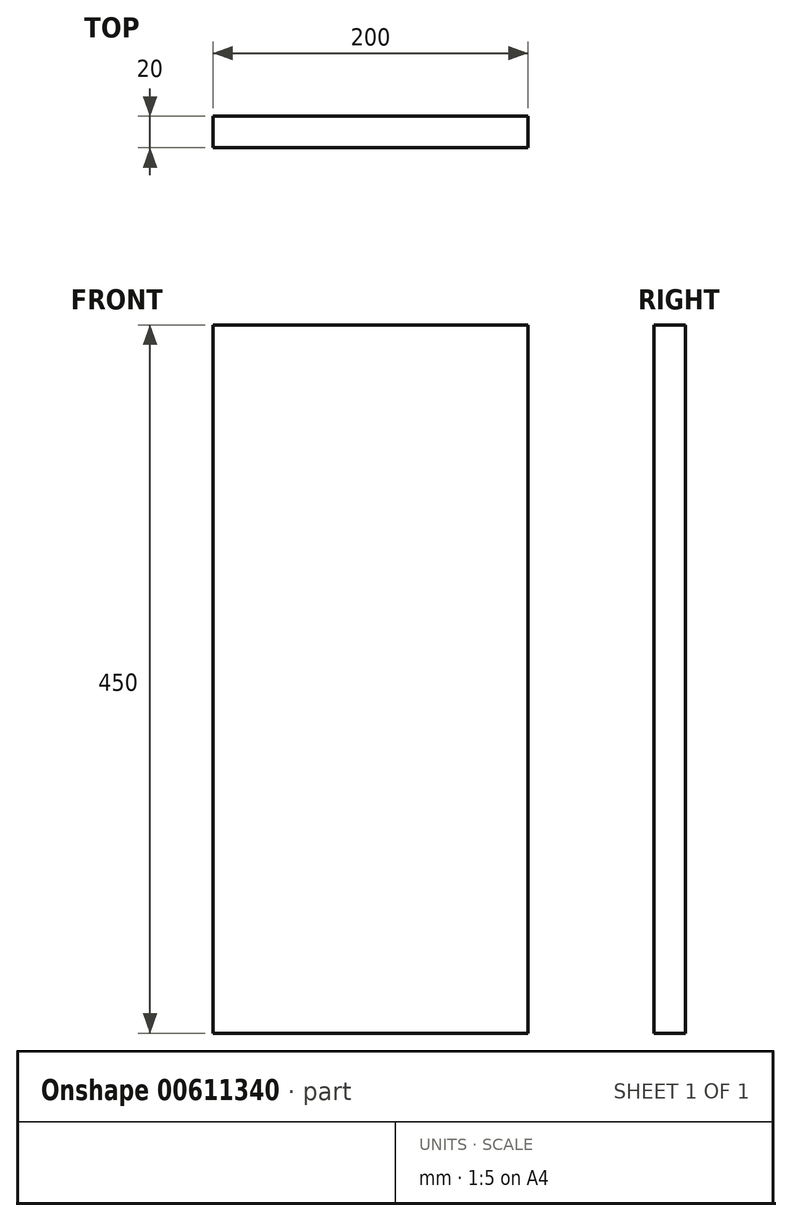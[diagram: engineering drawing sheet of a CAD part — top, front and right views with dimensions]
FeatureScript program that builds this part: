
annotation { "Feature Type Name" : "Feature", "Feature Type Description" : "" }
export const myFeature = defineFeature(function(context is Context, id is Id, definition is map)
    precondition{}
    {
        {
            var Q0;
            Q0=qCreatedBy(makeId("Front.planeOp"),FACE);
            var sketch = newSketch(context, id + "F0", { "sketchPlane" : qUnion([Q0])});
            skLineSegment(sketch, "E0.bottom", {"start": v(-100, 225) * mm, "end": v(100, 225) * mm});
            skLineSegment(sketch, "E0.top", {"start": v(-100, -225) * mm, "end": v(100, -225) * mm});
            skLineSegment(sketch, "E0.left", {"start": v(-100, 225) * mm, "end": v(-100, -225) * mm});
            skLineSegment(sketch, "E0.right", {"start": v(100, 225) * mm, "end": v(100, -225) * mm});
            skPoint(sketch, "E0.middle", {"position": v(0, 0) * mm});
            skSolve(sketch);
        }
        {
            var Q0;
            Q0=makeQuery(id+"F0.imprint","IMPRINT",FACE,{"disambiguationData":[TD([[makeQuery(id+"F0.imprint","IMPRINT",EDGE,{"derivedFrom":sQuery(id+"F0.wireOp",EDGE,"E0.bottom")}),-1.0]])]});
            extrude(context, id + "F1", {"entities" : qUnion([Q0]), "depth" : 20 * mm, "offsetDistance" : 25 * mm});
        }
    });
